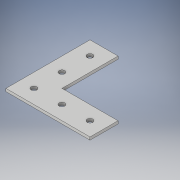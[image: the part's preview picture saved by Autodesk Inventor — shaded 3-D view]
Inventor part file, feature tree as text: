
AUTODESK INVENTOR PART (.ipt)
format: ipt  version: 2018 (Build 220112000, 112)  size: 122,368 bytes
history: native  units: in
note: dims shown in document units (in); Inventor stores cm internally (conversion verified against a paired STEP export)
features: extrude x1, sketch x1
ambient origin geometry x8: Origin, YZ Plane, XZ Plane, XY Plane, X Axis, Y Axis, Z Axis, Center Point
bodies: Solid1 (feature_tree)
feature tree (2):
  extrude  "Extrusion1"  Depth=1.0in
  sketch  "Sketch1"  dims[d0=0.0in d1=1.0in d2=3.0in d3=2.0in d4=1.0in d5=0.5in d6=0.5in d7=0.5in d8=0.5in d9=1.0in d10=1.0in d11=0.2031in d12=0.2031in d13=0.2031in d14=0.2031in d15=0.2031in d16=0.5in d17=0.5in d18=0.5in d19=1.0in d20=0.5in d21=0.1in d22=0.0in]
